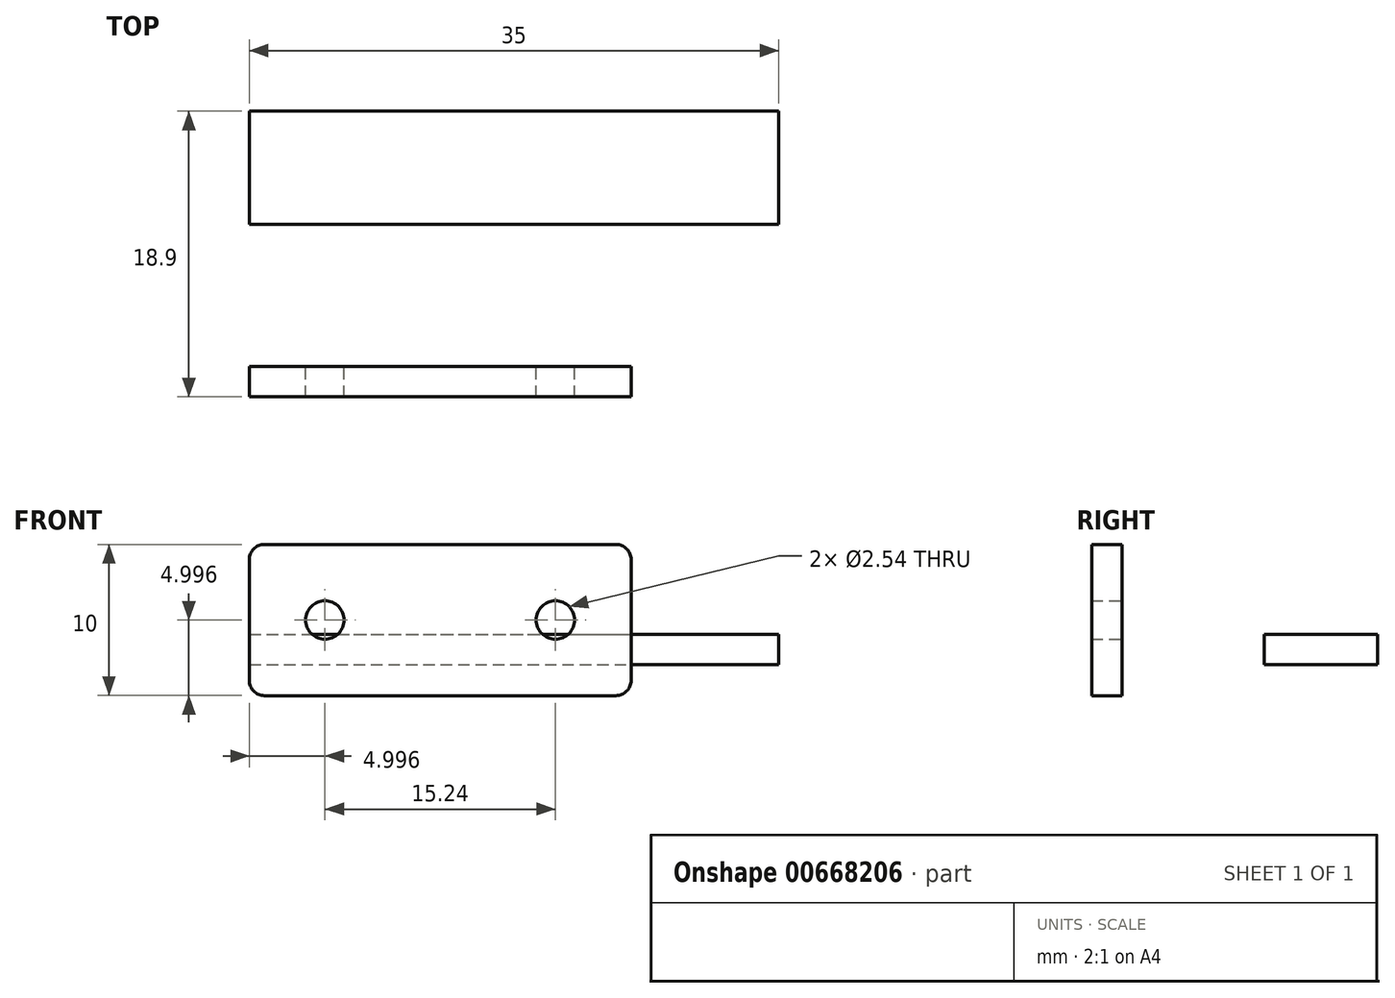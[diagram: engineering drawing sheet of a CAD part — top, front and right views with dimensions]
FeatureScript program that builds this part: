
annotation { "Feature Type Name" : "Feature", "Feature Type Description" : "" }
export const myFeature = defineFeature(function(context is Context, id is Id, definition is map)
    precondition{}
    {
        {
            var Q0;
            Q0=qCreatedBy(makeId("Front.planeOp"),FACE);
            var sketch = newSketch(context, id + "F0", { "sketchPlane" : qUnion([Q0])});
            skLineSegment(sketch, "E0.bottom", {"start": v(-18.96, 7.95) * mm, "end": v(4.28, 7.95) * mm});
            skLineSegment(sketch, "E0.top", {"start": v(-18.96, -2.05) * mm, "end": v(4.28, -2.05) * mm});
            skLineSegment(sketch, "E0.left", {"start": v(-19.96, 6.95) * mm, "end": v(-19.96, -1.05) * mm});
            skLineSegment(sketch, "E0.right", {"start": v(5.28, 6.95) * mm, "end": v(5.28, -1.05) * mm});
            skCircle(sketch, "E1", {"center": v(-14.96, 2.95) * mm, "radius": 1.27 * mm});
            skCircle(sketch, "E2", {"center": v(0.28, 2.95) * mm, "radius": 1.27 * mm});
            skPoint(sketch, "E3.visualSharp", {"position": v(-19.96, 7.95) * mm});
            skArc(sketch, "E3.filletArc", {"start": v(-18.96, 7.95) * mm, "mid": v(-19.67, 7.65) * mm, "end": v(-19.96, 6.95) * mm});
            skPoint(sketch, "E4.visualSharp", {"position": v(5.28, 7.95) * mm});
            skArc(sketch, "E4.filletArc", {"start": v(5.28, 6.95) * mm, "mid": v(4.98, 7.65) * mm, "end": v(4.28, 7.95) * mm});
            skPoint(sketch, "E5.visualSharp", {"position": v(5.28, -2.05) * mm});
            skArc(sketch, "E5.filletArc", {"start": v(4.28, -2.05) * mm, "mid": v(4.98, -1.76) * mm, "end": v(5.28, -1.05) * mm});
            skPoint(sketch, "E6.visualSharp", {"position": v(-19.96, -2.05) * mm});
            skArc(sketch, "E6.filletArc", {"start": v(-19.96, -1.05) * mm, "mid": v(-19.67, -1.76) * mm, "end": v(-18.96, -2.05) * mm});
            skSolve(sketch);
        }
        {
            var Q0;
            Q0=makeQuery(id+"F0.imprint","IMPRINT",FACE,{"disambiguationData":[TD([[makeQuery(id+"F0.imprint","IMPRINT",EDGE,{"derivedFrom":sQuery(id+"F0.wireOp",EDGE,"E0.bottom")}),-1.0]])]});
            extrude(context, id + "F1", {"entities" : qUnion([Q0]), "depth" : 2 * mm, "offsetDistance" : 25 * mm});
        }
        {
            var Q0;
            Q0=qCreatedBy(makeId("Top.planeOp"),FACE);
            var sketch = newSketch(context, id + "F2", { "sketchPlane" : qUnion([Q0])});
            skLineSegment(sketch, "E7.bottom", {"start": v(-19.96, 0) * mm, "end": v(15.04, 0) * mm});
            skLineSegment(sketch, "E7.top", {"start": v(-19.96, 7.5) * mm, "end": v(15.04, 7.5) * mm});
            skLineSegment(sketch, "E7.left", {"start": v(-19.96, 0) * mm, "end": v(-19.96, 7.5) * mm});
            skLineSegment(sketch, "E7.right", {"start": v(15.04, 0) * mm, "end": v(15.04, 7.5) * mm});
            skSolve(sketch);
        }
        {
            var Q0;
            Q0=qSketchRegion(id+"F2",true);
            extrude(context, id + "F3", {"entities" : qUnion([Q0]), "depth" : 2 * mm, "offsetDistance" : 25 * mm});
        }
        {
            var Q0;
            Q0=makeQuery(id+"F3.opExtrude","SWEPT_BODY",BODY,{"disambiguationData":[OSD([sQuery(id+"F2.wireOp",EDGE,"E7.bottom"),sQuery(id+"F2.wireOp",EDGE,"E7.top"),sQuery(id+"F2.wireOp",EDGE,"E7.left"),sQuery(id+"F2.wireOp",EDGE,"E7.right")])]});
            var Q1;
            Q1=makeQuery(id+"F3.opExtrude","SWEPT_EDGE",EDGE,{"disambiguationData":[OSD([sQuery(id+"F2.wireOp",EDGE,"E7.top"),sQuery(id+"F2.wireOp",EDGE,"E7.right")])]});
            var Q2;
            Q2=makeQuery(id+"F3.opExtrude","CAP_EDGE",EDGE,{"disambiguationData":[OSD([sQuery(id+"F2.wireOp",EDGE,"E7.top")])],"isStart":false});
            transform(context, id + "F4", {"entities" : qUnion([Q0]), "transformType" : TransformType.TRANSLATION_3D, "dx" : 0 * mm, "dy" : 9.4 * mm, "dz" : 0 * mm, "makeCopy" : false});
        }
    });
